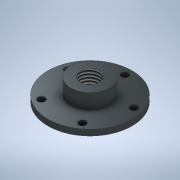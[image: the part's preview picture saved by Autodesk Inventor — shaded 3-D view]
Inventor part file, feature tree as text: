
AUTODESK INVENTOR PART (.ipt)
format: ipt  version: 2020 (Build 240168000, 168)  size: 151,552 bytes
history: native  units: mm
features: sketch x6, extrude x4, hole x2, thread x1
ambient origin geometry x8: Origin, YZ Plane, XZ Plane, XY Plane, X Axis, Y Axis, Z Axis, Center Point
bodies: Solid1 (feature_tree)
feature tree (13):
  extrude  "Extrusion1"  Depth=2.5mm TaperAngle=0.0deg
  extrude  "Extrusion2"  Depth=6.5mm TaperAngle=0.0deg
  extrude  "Extrusion3"  Depth=0.5mm TaperAngle=0.0deg
  extrude  "Extrusion6"  Depth=3.0mm
  hole  "Hole1"  [1 undecoded]
  hole  "Hole2"  [1 undecoded]
  thread  "Thread2"  [1 undecoded]
  sketch  "Sketch1"  dims[d0=35.0mm d1=2.5mm d2=0.0mm]
  sketch  "Sketch2"  dims[d3=16.0mm d4=6.5mm d5=0.0mm]
  sketch  "Sketch3"  dims[d6=19.0mm d7=0.5mm d8=0.0mm]
  sketch  "Sketch6"  dims[d17=3.0mm d18=14.5mm]
  sketch  "Sketch7"  dims[d19=50.0mm d21=360.0deg d23=0.0mm d24=0.0mm]
  sketch  "Sketch8"  dims[d25=8.0mm d26=6.0mm d27=4.0mm d28=2.0mm d29=90.0deg d30=7.0mm d31=20.594885mm d32=4.0mm d33=6.0mm d34=4.0mm d35=2.0mm d36=90.0deg d37=7.0mm d38=20.594885mm d39=7.0mm d40=0.0mm]
note: 3 required parameter values undecoded (feature->parameter linkage not recoverable at this tier; creation-order binding heuristic only, values carry confidence <= 0.55)
